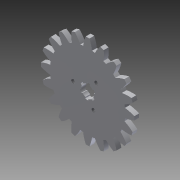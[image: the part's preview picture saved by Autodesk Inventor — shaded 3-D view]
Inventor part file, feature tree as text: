
AUTODESK INVENTOR PART (.ipt)
format: ipt  version: 2014 SP1 (Build 180222100, 222)  size: 281,600 bytes
history: native  units: in
note: dims shown in document units (in); Inventor stores cm internally (conversion verified against a paired STEP export)
features: reference x22, extrude x3, thread x3, sketch x3
ambient origin geometry x8: Origin, YZ Plane, XZ Plane, XY Plane, X Axis, Y Axis, Z Axis, Center Point
bodies: Solid1 (feature_tree)
feature tree (31):
  extrude  "Extrusion1"  Depth=0.25in TaperAngle=0.0deg
  extrude  "Extrusion2"  Depth=1.0in TaperAngle=0.0deg
  extrude  "Extrusion3"  Depth=1.0in TaperAngle=0.0deg
  thread  "Thread1"  [1 undecoded]
  thread  "Thread2"  [1 undecoded]
  thread  "Thread3"  [1 undecoded]
  sketch  "Sketch1"  dims[d0=0.25in d1=0.0in d2=1.0in d3=0.0in]
  sketch  "Sketch2"  dims[d4=1.0in d5=0.0in d6=1.0in d7=0.0in]
  reference  "Reference1"
  reference  "Reference2"
  reference  "Reference3"
  reference  "Reference4"
  reference  "Reference5"
  reference  "Reference6"
  reference  "Reference7"
  reference  "Reference8"
  reference  "Reference9"
  reference  "Reference10"
  reference  "Reference11"
  reference  "Reference12"
  reference  "Reference13"
  reference  "Reference14"
  reference  "Reference15"
  reference  "Reference16"
  reference  "Reference17"
  reference  "Reference18"
  reference  "Reference19"
  sketch  "Sketch3"  dims[d8=1.0in d9=0.0in d10=1.0in d11=0.0in]
  reference  "Reference20"
  reference  "Reference21"
  reference  "Reference22"
note: 3 required parameter values undecoded (feature->parameter linkage not recoverable at this tier; creation-order binding heuristic only, values carry confidence <= 0.55)
